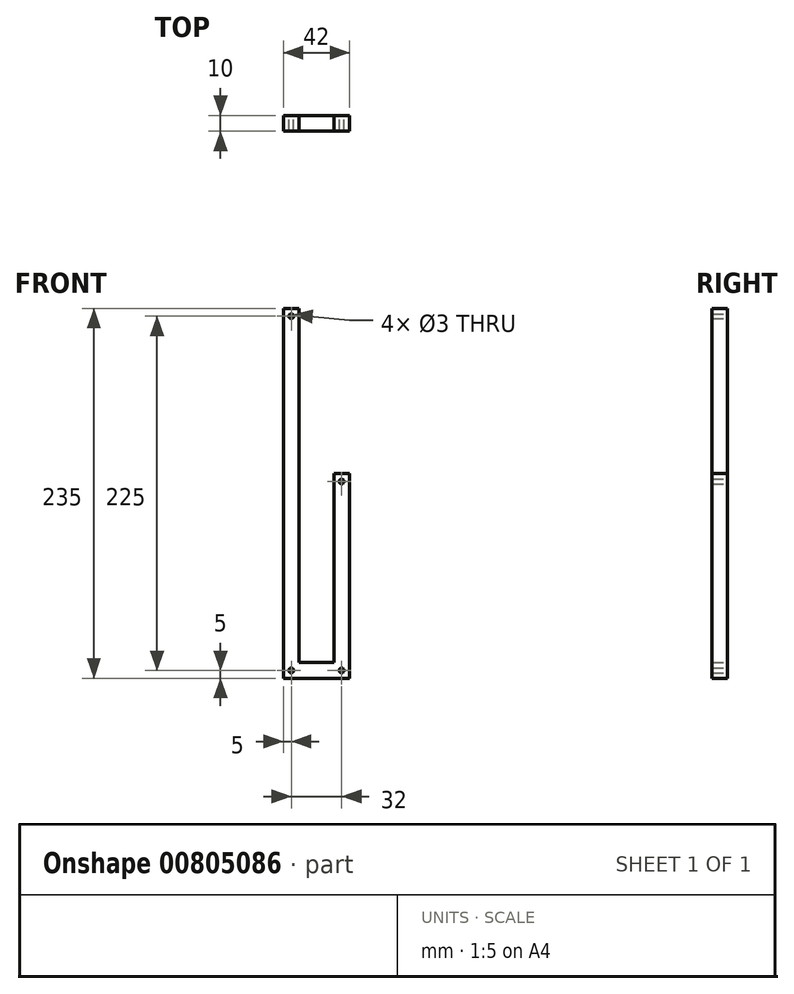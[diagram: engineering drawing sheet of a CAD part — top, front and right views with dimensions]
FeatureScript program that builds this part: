
annotation { "Feature Type Name" : "Feature", "Feature Type Description" : "" }
export const myFeature = defineFeature(function(context is Context, id is Id, definition is map)
    precondition{}
    {
        {
            var Q0;
            Q0=qCreatedBy(makeId("Front.planeOp"),FACE);
            var sketch = newSketch(context, id + "F0", { "sketchPlane" : qUnion([Q0])});
            skLineSegment(sketch, "E0.bottom", {"start": v(0, 147.89) * mm, "end": v(10, 147.89) * mm});
            skLineSegment(sketch, "E0.top", {"start": v(0, -87.11) * mm, "end": v(10, -87.11) * mm});
            skLineSegment(sketch, "E0.left", {"start": v(0, 147.89) * mm, "end": v(0, -87.11) * mm});
            skLineSegment(sketch, "E0.right", {"start": v(10, 147.89) * mm, "end": v(10, -87.11) * mm});
            skLineSegment(sketch, "E1.bottom", {"start": v(10, -87.11) * mm, "end": v(32, -87.11) * mm});
            skLineSegment(sketch, "E1.top", {"start": v(10, -77.11) * mm, "end": v(35, -77.11) * mm});
            skLineSegment(sketch, "E1.left", {"start": v(10, -87.11) * mm, "end": v(10, -77.11) * mm});
            skCircle(sketch, "E2", {"center": v(5, 142.89) * mm, "radius": 1.5 * mm});
            skPoint(sketch, "E2.centerSnap0", {"position": v(5, 147.89) * mm});
            skCircle(sketch, "E3", {"center": v(5, -82.11) * mm, "radius": 1.5 * mm});
            skPoint(sketch, "E3.centerSnap0", {"position": v(5, -87.11) * mm});
            skLineSegment(sketch, "E4.bottom", {"start": v(32, 42.89) * mm, "end": v(42, 42.89) * mm});
            skLineSegment(sketch, "E4.top", {"start": v(32, -87.11) * mm, "end": v(42, -87.11) * mm});
            skLineSegment(sketch, "E4.left", {"start": v(32, 42.89) * mm, "end": v(32, -87.11) * mm});
            skLineSegment(sketch, "E4.right", {"start": v(42, 42.89) * mm, "end": v(42, -87.11) * mm});
            skCircle(sketch, "E5", {"center": v(37, -82.11) * mm, "radius": 1.5 * mm});
            skCircle(sketch, "E6", {"center": v(37, 37.89) * mm, "radius": 1.5 * mm});
            skPoint(sketch, "E7", {"position": v(37, 42.89) * mm});
            skSolve(sketch);
        }
        {
            var Q0;
            Q0=makeQuery(id+"F0.imprint","IMPRINT",FACE,{"disambiguationData":[TD([[makeQuery(id+"F0.imprint","IMPRINT",EDGE,{"derivedFrom":sQuery(id+"F0.wireOp",EDGE,"E0.bottom")}),-1.0]])]});
            var Q1;
            {var subQ0=sQuery(id+"F0.wireOp",EDGE,"E1.bottom");Q1=makeQuery(id+"F0.imprint","IMPRINT",FACE,{"disambiguationData":[TD([[makeQuery(id+"F0.imprint","IMPRINT",EDGE,{"derivedFrom":subQ0}),1.0]])]});}
            var Q2;
            {var subQ3=sQuery(id+"F0.wireOp",EDGE,"3u374LFE-TpTa-H1pT-iGOS-Nu6D7jWMxNXw.bottom");Q2=makeQuery(id+"F0.imprint","IMPRINT",FACE,{"disambiguationData":[TD([[makeQuery(id+"F0.imprint","IMPRINT",EDGE,{"derivedFrom":subQ3}),1.0]])]});}
            var Q3;
            {var subQ3=sQuery(id+"F0.wireOp",EDGE,"E4.bottom");Q3=makeQuery(id+"F0.imprint","IMPRINT",FACE,{"disambiguationData":[TD([[makeQuery(id+"F0.imprint","IMPRINT",EDGE,{"derivedFrom":subQ3}),-1.0]])]});}
            extrude(context, id + "F1", {"entities" : qUnion([Q0, Q1, Q2, Q3]), "endBound" : BoundingType.SYMMETRIC, "depth" : 10 * mm, "offsetDistance" : 25.4 * mm});
        }
        {
            var Q0;
            Q0=makeQuery(id+"F0.imprint","IMPRINT",FACE,{"disambiguationData":[TD([[makeQuery(id+"F0.imprint","IMPRINT",EDGE,{"derivedFrom":sQuery(id+"F0.wireOp",EDGE,"E3")}),1.0]])]});
            var Q1;
            Q1=makeQuery(id+"F0.imprint","IMPRINT",FACE,{"disambiguationData":[TD([[makeQuery(id+"F0.imprint","IMPRINT",EDGE,{"derivedFrom":sQuery(id+"F0.wireOp",EDGE,"E5")}),1.0]])]});
            var Q2;
            Q2=makeQuery(id+"F0.imprint","IMPRINT",FACE,{"disambiguationData":[TD([[makeQuery(id+"F0.imprint","IMPRINT",EDGE,{"derivedFrom":sQuery(id+"F0.wireOp",EDGE,"E6")}),1.0]])]});
            var Q3;
            Q3=makeQuery(id+"F0.imprint","IMPRINT",FACE,{"disambiguationData":[TD([[makeQuery(id+"F0.imprint","IMPRINT",EDGE,{"derivedFrom":sQuery(id+"F0.wireOp",EDGE,"E2")}),1.0]])]});
            var Q4;
            Q4=qCreatedBy(makeId("Front.planeOp"),FACE);
            extrude(context, id + "F2", {"entities" : qUnion([Q0, Q1, Q2, Q3]), "operationType" : NewBodyOperationType.REMOVE, "endBound" : BoundingType.SYMMETRIC, "depth" : 10 * mm, "endBoundEntityFace" : qUnion([Q4]), "offsetDistance" : 25.4 * mm});
        }
    });
